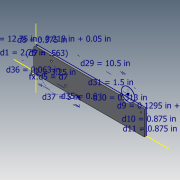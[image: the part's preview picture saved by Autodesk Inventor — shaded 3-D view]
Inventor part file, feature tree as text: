
AUTODESK INVENTOR PART (.ipt)
format: ipt  version: 2018.3 (Build 223284000, 284)  size: 144,896 bytes
history: native  units: in
note: dims shown in document units (in); Inventor stores cm internally (conversion verified against a paired STEP export)
features: sketch x2, extrude x2, hole x2, fillet x2
ambient origin geometry x8: Origin, YZ Plane, XZ Plane, XY Plane, X Axis, Y Axis, Z Axis, Center Point
bodies: Solid1 (feature_tree)
feature tree (8):
  sketch  "Sketch1"  dims[d0=12.582in d1=2.75in]
  extrude  "Extrusion1"  Depth=2.75in
  hole  "Hole1"  [1 undecoded]
  hole  "Hole2"  [1 undecoded]
  fillet  "Fillet1"  Radius=0.375in
  extrude  "Extrusion2"  Depth=5.0in
  fillet  "Fillet2"  Radius=0.875in
  sketch  "Sketch2"  dims[d2=3.25in d5=0.5625in d7=0.5625in d8=0.375in d9=0.3595in d10=0.875in d11=0.875in d12=0.23in d13=0.0in d14=0.15in d15=0.75in d16=0.375in d17=0.25in d18=0.5635in d19=1.0in d20=0.8108in d21=0.22in d22=0.75in d23=0.375in d24=0.25in d25=0.5635in d26=1.0in d27=0.8108in d28=0.25in d29=10.5in d30=0.313in d31=1.5in d32=1.0in d33=0.0in d34=0.125in d35=0.6in d36=0.063in d37=5.0in]
note: 2 required parameter values undecoded (feature->parameter linkage not recoverable at this tier; creation-order binding heuristic only, values carry confidence <= 0.55)
